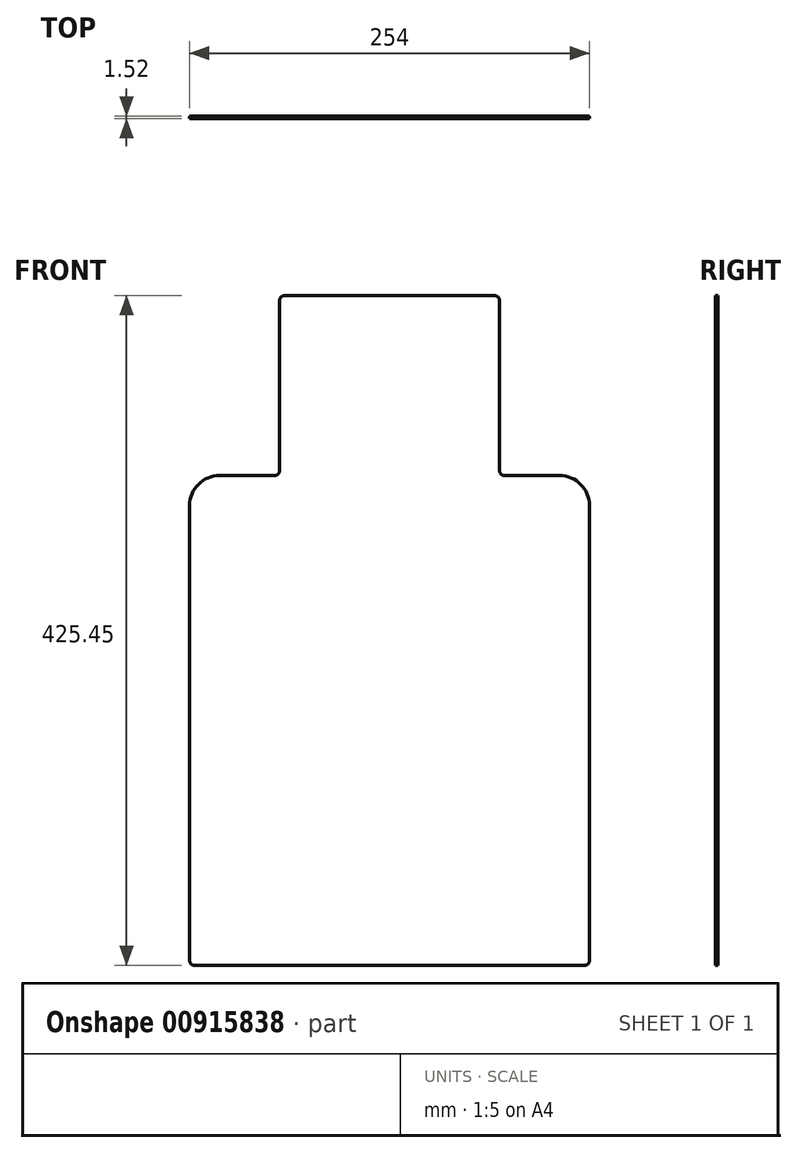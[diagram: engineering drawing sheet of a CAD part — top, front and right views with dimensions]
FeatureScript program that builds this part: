
annotation { "Feature Type Name" : "Feature", "Feature Type Description" : "" }
export const myFeature = defineFeature(function(context is Context, id is Id, definition is map)
    precondition{}
    {
        {
            var Q0;
            Q0=qCreatedBy(makeId("Front.planeOp"),FACE);
            var sketch = newSketch(context, id + "F0", { "sketchPlane" : qUnion([Q0])});
            skLineSegment(sketch, "E0", {"start": v(3.18, 0) * mm, "end": v(250.83, 0) * mm});
            skLineSegment(sketch, "E1", {"start": v(254, 3.18) * mm, "end": v(254, 292.1) * mm});
            skLineSegment(sketch, "E2", {"start": v(234.95, 311.15) * mm, "end": v(200.03, 311.15) * mm});
            skLineSegment(sketch, "E3", {"start": v(196.85, 314.32) * mm, "end": v(196.85, 422.28) * mm});
            skLineSegment(sketch, "E4", {"start": v(193.67, 425.45) * mm, "end": v(60.32, 425.45) * mm});
            skLineSegment(sketch, "E5", {"start": v(57.15, 422.28) * mm, "end": v(57.15, 314.33) * mm});
            skLineSegment(sketch, "E6", {"start": v(53.98, 311.15) * mm, "end": v(19.05, 311.15) * mm});
            skLineSegment(sketch, "E7", {"start": v(0, 292.1) * mm, "end": v(0, 3.18) * mm});
            skPoint(sketch, "E8.visualSharp", {"position": v(0, 311.15) * mm});
            skArc(sketch, "E9.filletArc", {"start": v(19.05, 311.15) * mm, "mid": v(5.58, 305.57) * mm, "end": v(0, 292.1) * mm});
            skPoint(sketch, "E10.visualSharp", {"position": v(254, 311.15) * mm});
            skArc(sketch, "E10.filletArc", {"start": v(254, 292.1) * mm, "mid": v(248.42, 305.57) * mm, "end": v(234.95, 311.15) * mm});
            skPoint(sketch, "E11.visualSharp", {"position": v(196.85, 311.15) * mm});
            skArc(sketch, "E11.filletArc", {"start": v(196.85, 314.32) * mm, "mid": v(197.78, 312.08) * mm, "end": v(200.03, 311.15) * mm});
            skPoint(sketch, "E12.visualSharp", {"position": v(57.15, 311.15) * mm});
            skArc(sketch, "E12.filletArc", {"start": v(53.98, 311.15) * mm, "mid": v(56.22, 312.08) * mm, "end": v(57.15, 314.33) * mm});
            skPoint(sketch, "E13.visualSharp", {"position": v(0, 0) * mm});
            skArc(sketch, "E13.filletArc", {"start": v(0, 3.18) * mm, "mid": v(0.93, 0.93) * mm, "end": v(3.18, 0) * mm});
            skPoint(sketch, "E14.visualSharp", {"position": v(254, 0) * mm});
            skArc(sketch, "E14.filletArc", {"start": v(250.83, 0) * mm, "mid": v(253.07, 0.93) * mm, "end": v(254, 3.18) * mm});
            skPoint(sketch, "E15.visualSharp", {"position": v(57.15, 425.45) * mm});
            skArc(sketch, "E15.filletArc", {"start": v(60.32, 425.45) * mm, "mid": v(58.08, 424.52) * mm, "end": v(57.15, 422.28) * mm});
            skPoint(sketch, "E16.visualSharp", {"position": v(196.85, 425.45) * mm});
            skArc(sketch, "E16.filletArc", {"start": v(196.85, 422.28) * mm, "mid": v(195.92, 424.52) * mm, "end": v(193.67, 425.45) * mm});
            skSolve(sketch);
        }
        {
            var Q0;
            Q0=makeQuery(id+"F0.imprint","IMPRINT",FACE,{"disambiguationData":[TD([[makeQuery(id+"F0.imprint","IMPRINT",EDGE,{"derivedFrom":sQuery(id+"F0.wireOp",EDGE,"E0")}),1.0]])]});
            extrude(context, id + "F1", {"entities" : qUnion([Q0]), "depth" : 1.52 * mm, "offsetDistance" : 25.4 * mm});
        }
    });
